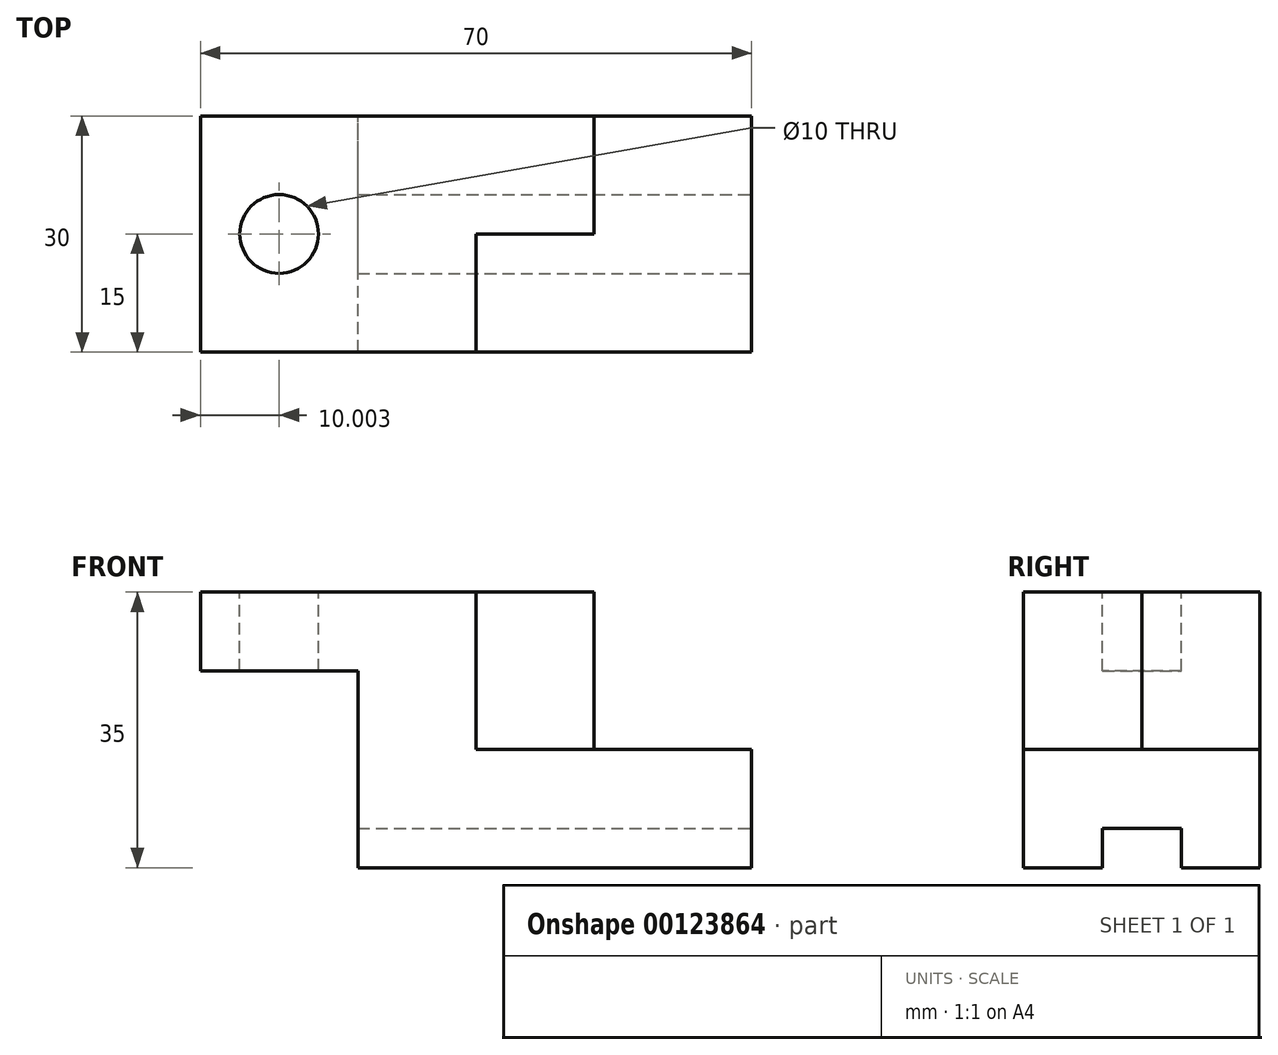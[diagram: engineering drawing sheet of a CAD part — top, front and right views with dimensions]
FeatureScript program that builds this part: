
annotation { "Feature Type Name" : "Feature", "Feature Type Description" : "" }
export const myFeature = defineFeature(function(context is Context, id is Id, definition is map)
    precondition{}
    {
        {
            var Q0;
            Q0=qCreatedBy(makeId("Top.planeOp"),FACE);
            var sketch = newSketch(context, id + "F0", { "sketchPlane" : qUnion([Q0])});
            skLineSegment(sketch, "E0.bottom", {"start": v(-25.22, -15.41) * mm, "end": v(24.78, -15.41) * mm});
            skLineSegment(sketch, "E0.top", {"start": v(-25.22, 14.59) * mm, "end": v(24.78, 14.59) * mm});
            skLineSegment(sketch, "E0.left", {"start": v(-25.22, -15.41) * mm, "end": v(-25.22, 14.59) * mm});
            skLineSegment(sketch, "E0.right", {"start": v(24.78, -15.41) * mm, "end": v(24.78, 14.59) * mm});
            skSolve(sketch);
        }
        {
            var Q0;
            Q0 = qSketchRegion(id + "F0", true);
            extrude(context, id + "F1", {"entities" : qUnion([Q0]), "depth" : 15 * mm});
        }
        {
            var Q0;
            Q0=makeQuery(id+"F1.opExtrude","SWEPT_FACE",FACE,{"disambiguationData":[OSD([sQuery(id+"F0.wireOp",EDGE,"E0.right")])]});
            var sketch = newSketch(context, id + "F2", { "sketchPlane" : qUnion([Q0])});
            skLineSegment(sketch, "E1", {"start": v(-5.41, 0) * mm, "end": v(-5.41, 5) * mm});
            skLineSegment(sketch, "E2", {"start": v(-5.41, 5) * mm, "end": v(4.59, 5) * mm});
            skLineSegment(sketch, "E3", {"start": v(4.59, 5) * mm, "end": v(4.59, 0) * mm});
            skSolve(sketch);
        }
        {
            var Q0;
            Q0 = qSketchRegion(id + "F2", true);
            var Q1;
            {var subQ0=sQuery(id+"F2.wireOp",EDGE,"E1");Q1=makeQuery(id+"F2.imprint","IMPRINT",FACE,{"disambiguationData":[TD([[makeQuery(id+"F2.imprint","IMPRINT",EDGE,{"derivedFrom":subQ0}),-1.0]])]});}
            extrude(context, id + "F3", {"entities" : qUnion([Q0, Q1]), "operationType" : NewBodyOperationType.REMOVE, "oppositeDirection" : true, "depth" : 50 * mm});
        }
        {
            var Q0;
            Q0=makeQuery(id+"F1.opExtrude","CAP_FACE",FACE,{"disambiguationData":[OSD([sQuery(id+"F0.wireOp",EDGE,"E0.bottom"),sQuery(id+"F0.wireOp",EDGE,"E0.top"),sQuery(id+"F0.wireOp",EDGE,"E0.left"),sQuery(id+"F0.wireOp",EDGE,"E0.right")])],"isStart":false});
            var sketch = newSketch(context, id + "F4", { "sketchPlane" : qUnion([Q0])});
            skLineSegment(sketch, "E4", {"start": v(-25.22, -15.41) * mm, "end": v(-10.22, -15.41) * mm});
            skLineSegment(sketch, "E5", {"start": v(-10.22, -15.41) * mm, "end": v(-10.22, -0.41) * mm});
            skLineSegment(sketch, "E6", {"start": v(-10.22, -0.41) * mm, "end": v(4.78, -0.41) * mm});
            skLineSegment(sketch, "E7", {"start": v(4.78, -0.41) * mm, "end": v(4.78, 14.59) * mm});
            skSolve(sketch);
        }
        {
            var Q0;
            Q0 = qSketchRegion(id + "F4", true);
            var Q1;
            Q1=makeQuery(id+"F4.imprint","IMPRINT",FACE,{"disambiguationData":[TD([[makeQuery(id+"F4.imprint","IMPRINT",EDGE,{"derivedFrom":sQuery(id+"F4.wireOp",EDGE,"E4")}),1.0]])]});
            extrude(context, id + "F5", {"entities" : qUnion([Q0, Q1]), "operationType" : NewBodyOperationType.ADD, "depth" : 10 * mm});
        }
        {
            var Q0;
            Q0=makeQuery(id+"F5.opExtrude","CAP_FACE",FACE,{"disambiguationData":[OSD([sQuery(id+"F0.wireOp",EDGE,"E0.top"),sQuery(id+"F0.wireOp",EDGE,"E0.left"),sQuery(id+"F4.wireOp",EDGE,"E4"),sQuery(id+"F4.wireOp",EDGE,"E5"),sQuery(id+"F4.wireOp",EDGE,"E6"),sQuery(id+"F4.wireOp",EDGE,"E7")])],"isStart":false});
            var sketch = newSketch(context, id + "F6", { "sketchPlane" : qUnion([Q0])});
            skLineSegment(sketch, "E8", {"start": v(-25.22, -15.41) * mm, "end": v(-45.22, -15.41) * mm});
            skLineSegment(sketch, "E9", {"start": v(-45.22, -15.41) * mm, "end": v(-45.22, 14.59) * mm});
            skLineSegment(sketch, "E10", {"start": v(-45.22, 14.59) * mm, "end": v(-25.22, 14.59) * mm});
            skSolve(sketch);
        }
        {
            var Q0;
            Q0 = qSketchRegion(id + "F6", true);
            var Q1;
            Q1=makeQuery(id+"F6.imprint","IMPRINT",FACE,{"disambiguationData":[TD([[makeQuery(id+"F6.imprint","IMPRINT",EDGE,{"derivedFrom":sQuery(id+"F6.wireOp",EDGE,"E8")}),-1.0]])]});
            var Q2;
            Q2=makeQuery(id+"F6.imprint","IMPRINT",FACE,{"disambiguationData":[TD([[makeQuery(id+"F6.imprint","IMPRINT",EDGE,{"derivedFrom":makeQuery(id+"F5.opExtrude","CAP_EDGE",EDGE,{"disambiguationData":[OSD([sQuery(id+"F4.wireOp",EDGE,"E4")])],"isStart":false})}),1.0]])]});
            extrude(context, id + "F7", {"entities" : qUnion([Q0, Q1, Q2]), "operationType" : NewBodyOperationType.ADD, "depth" : 10 * mm});
        }
        {
            var Q0;
            Q0=makeQuery(id+"F7.opExtrude","CAP_FACE",FACE,{"disambiguationData":[OSD([sQuery(id+"F0.wireOp",EDGE,"E0.top"),sQuery(id+"F4.wireOp",EDGE,"E4"),sQuery(id+"F4.wireOp",EDGE,"E5"),sQuery(id+"F4.wireOp",EDGE,"E6"),sQuery(id+"F4.wireOp",EDGE,"E7"),sQuery(id+"F6.wireOp",EDGE,"E8"),sQuery(id+"F6.wireOp",EDGE,"E9"),sQuery(id+"F6.wireOp",EDGE,"E10")])],"isStart":false});
            var sketch = newSketch(context, id + "F8", { "sketchPlane" : qUnion([Q0])});
            skLineSegment(sketch, "E11", {"start": v(-45.22, -0.41) * mm, "end": v(-35.22, -0.41) * mm, "construction": true});
            skLineSegment(sketch, "E12", {"start": v(-35.22, -0.41) * mm, "end": v(-35.22, -15.41) * mm, "construction": true});
            skCircle(sketch, "E13", {"center": v(-35.22, -0.41) * mm, "radius": 5 * mm});
            skSolve(sketch);
        }
        {
            var Q0;
            Q0=makeQuery(id+"F8.imprint","IMPRINT",FACE,{"disambiguationData":[TD([[makeQuery(id+"F8.imprint","IMPRINT",EDGE,{"derivedFrom":sQuery(id+"F8.wireOp",EDGE,"E13")}),1.0]])]});
            extrude(context, id + "F9", {"entities" : qUnion([Q0]), "operationType" : NewBodyOperationType.REMOVE, "oppositeDirection" : true, "depth" : 25 * mm});
        }
    });
